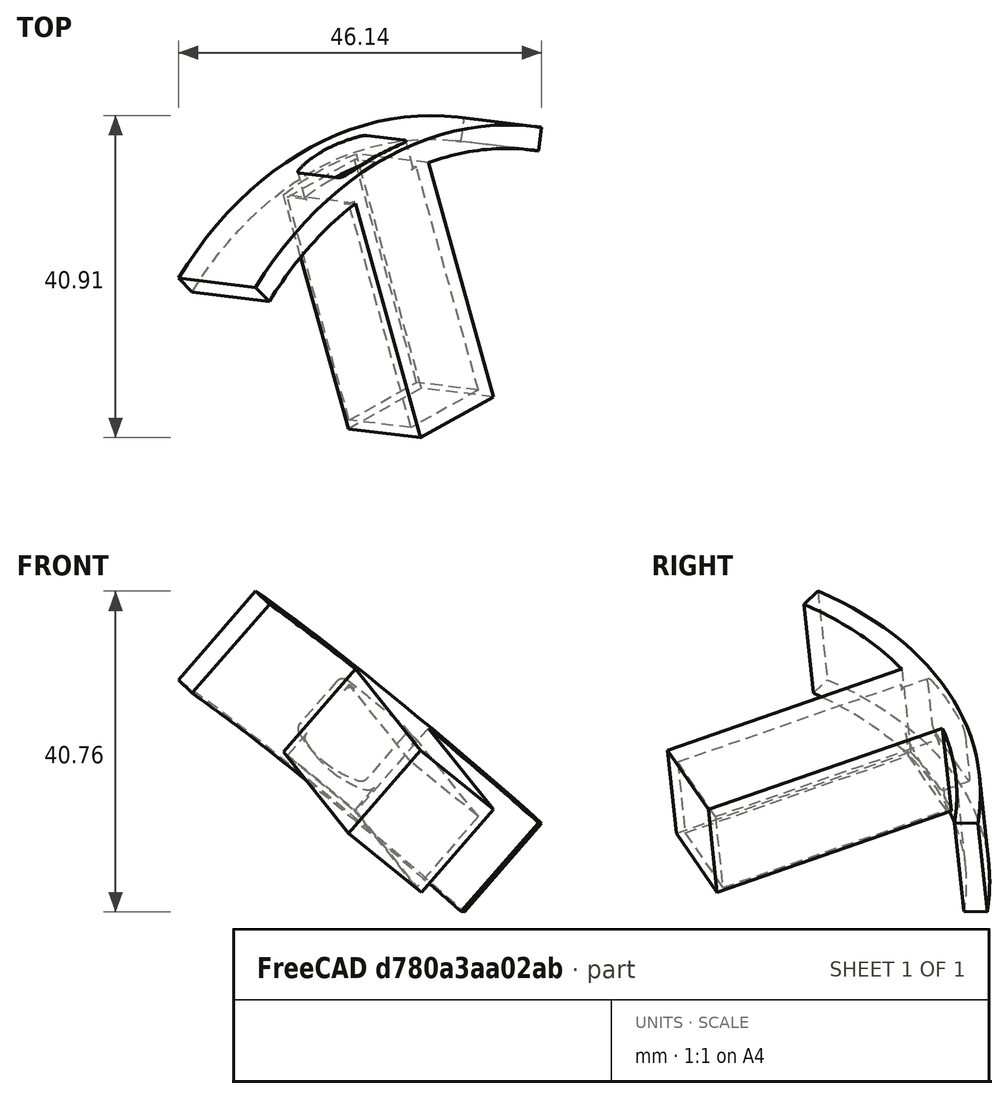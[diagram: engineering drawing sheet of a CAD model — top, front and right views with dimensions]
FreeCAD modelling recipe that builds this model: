
FCSTD DOCUMENT  (FreeCAD 0.16R4924 (Git))
Label: interior_servo_bay_v3p1
License: All rights reserved
LicenseURL: http://en.wikipedia.org/wiki/All_rights_reserved
objects: Part::Cut×3, Part::Cylinder×2, Part::Feature×2, Part::Extrusion×2, Part::MultiFuse×2, Part::Box×2, Part::Thickness×1, App::MeasureDistance×1
note: 14 computed .brp shape members not serialized (recipe doc carries the construction recipe); baked Part::Feature solids carry a one-line shape summary decoded from their .brp

FEATURE [Part::Cylinder] Cylinder  label="bottle_wall"
  Angle = 60
  Height = 15
  Placement = pos=(8.5,-7,0) rot=(0,0,1;1.0472rad)
  Radius = 51
FEATURE [Part::Cylinder] Cylinder001  label="bottle_wall001"
  Angle = 60
  Height = 15
  Placement = pos=(8.5,-7,0) rot=(0,0,1;1.0472rad)
  Radius = 48
FEATURE [Part::Cut] Cut  label="bottle_wall_composite"
  Base = -> Cylinder
  Placement = pos=(0,-2,0) rot=(0,0,1;0rad)
  Tool = -> Cylinder001
FEATURE [Part::Feature] Common_cs  label="pin_cs"
  Placement = pos=(3.5,35,2) rot=(0,0,1;0rad)
  shape: bbox 10 x 2e-07 x 8 mm, 0 faces, 0 solids (baked)
FEATURE [Part::Extrusion] Extrude
  Base = -> Common_cs
  Dir = (0,5,0)
  Solid = true
FEATURE [Part::Thickness] Thickness
  Faces = -> Extrude [Face7]
  Intersection = false
  Join = 0
  Mode = 0
  SelfIntersection = false
  Value = 1
FEATURE [Part::Feature] Common_cs001  label="pin_cs001"
  Placement = pos=(3.5,35,2) rot=(0,0,1;0rad)
  shape: bbox 10 x 2e-07 x 8 mm, 0 faces, 0 solids (baked)
FEATURE [Part::Extrusion] Extrude001
  Base = -> Common_cs001
  Dir = (0,5,0)
  Solid = true
FEATURE [Part::MultiFuse] Fusion  label="bolt_bottle_side_opening"
  Placement = pos=(0,-7,1) rot=(0,0,1;0rad)
  Shapes = -> [Thickness,Extrude,Extrude001]
FEATURE [Part::Box] Box  label="pullBay"
  Height = 15
  Length = 12
  Placement = pos=(2.5,7,2) rot=(0,0,1;0rad)
  Width = 31
FEATURE [Part::Box] Box001  label="Case"
  Height = 14
  Length = 13
  Placement = pos=(2,6,0) rot=(0,0,1;0rad)
  Width = 34
FEATURE [Part::Cut] Cut001  label="cut bay from case"
  Base = -> Box001
  Tool = -> Box
FEATURE [Part::MultiFuse] Fusion001  label="wall plus case"
  Shapes = -> [Cut,Cut001]
FEATURE [Part::Cut] Cut002  label="hole cut out of case"
  Base = -> Fusion001
  Placement = pos=(0,0,0) rot=(-0.188305,0.975433,0.114334;3.82553rad)
  Tool = -> Fusion
FEATURE [App::MeasureDistance] Distance  label="Distance: 25.508"
  Distance = 25.5079
  P1 = (-6.57223,30.2874,35.1369)
  P2 = (-4.39791,5.35164,30.2241)
